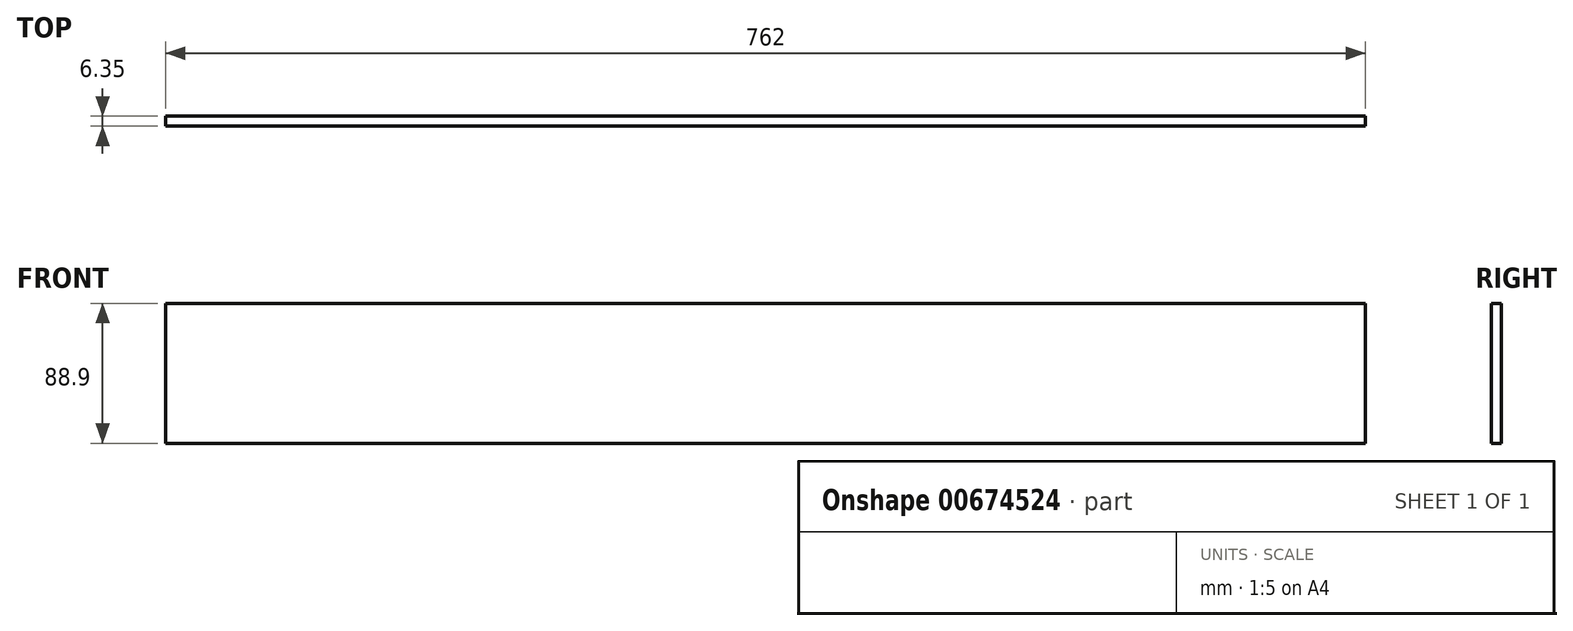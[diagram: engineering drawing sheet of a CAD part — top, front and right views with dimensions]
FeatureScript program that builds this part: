
annotation { "Feature Type Name" : "Feature", "Feature Type Description" : "" }
export const myFeature = defineFeature(function(context is Context, id is Id, definition is map)
    precondition{}
    {
        {
            var Q0;
            Q0=qCreatedBy(makeId("Front.planeOp"),FACE);
            var sketch = newSketch(context, id + "F0", { "sketchPlane" : qUnion([Q0])});
            skLineSegment(sketch, "E0.bottom", {"start": v(703.54, 41.54) * mm, "end": v(-58.46, 41.54) * mm});
            skLineSegment(sketch, "E0.top", {"start": v(703.54, -47.36) * mm, "end": v(-58.46, -47.36) * mm});
            skLineSegment(sketch, "E0.left", {"start": v(703.54, 41.54) * mm, "end": v(703.54, -47.36) * mm});
            skLineSegment(sketch, "E0.right", {"start": v(-58.46, 41.54) * mm, "end": v(-58.46, -47.36) * mm});
            skPoint(sketch, "E0.middle", {"position": v(322.54, -2.91) * mm});
            skSolve(sketch);
        }
        {
            var Q0;
            Q0 = qSketchRegion(id + "F0", true);
            extrude(context, id + "F1", {"entities" : qUnion([Q0]), "depth" : 6.35 * mm, "offsetDistance" : 25.4 * mm});
        }
    });
